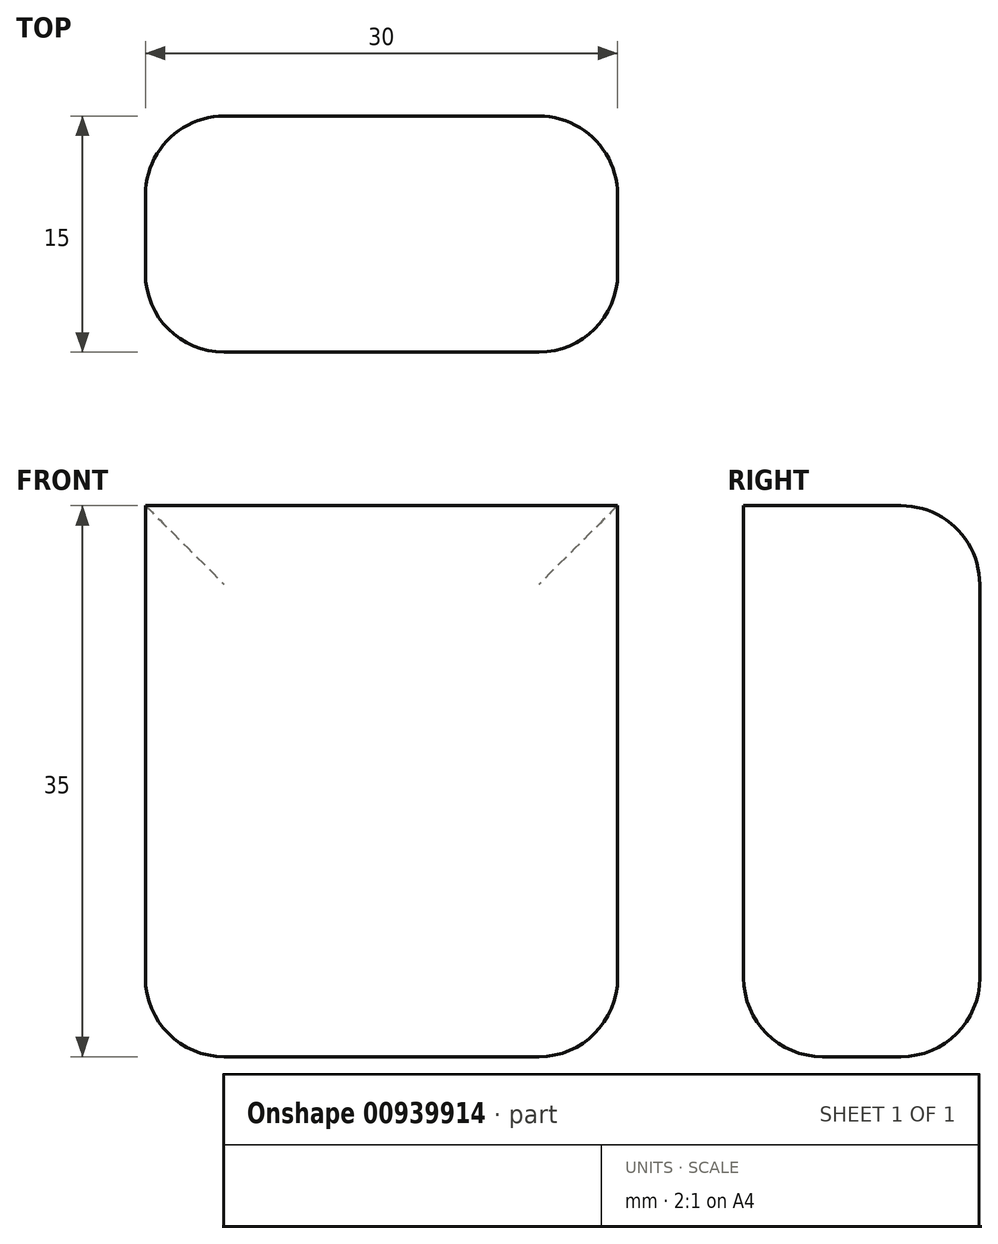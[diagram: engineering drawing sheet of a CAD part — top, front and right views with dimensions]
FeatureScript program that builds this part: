
annotation { "Feature Type Name" : "Feature", "Feature Type Description" : "" }
export const myFeature = defineFeature(function(context is Context, id is Id, definition is map)
    precondition{}
    {
        {
            var Q0;
            Q0=qCreatedBy(makeId("Front.planeOp"),FACE);
            var sketch = newSketch(context, id + "F0", { "sketchPlane" : qUnion([Q0])});
            skLineSegment(sketch, "E0.bottom", {"start": v(-15, 17.5) * mm, "end": v(15, 17.5) * mm});
            skLineSegment(sketch, "E0.top", {"start": v(-15, -17.5) * mm, "end": v(15, -17.5) * mm});
            skLineSegment(sketch, "E0.left", {"start": v(-15, 17.5) * mm, "end": v(-15, -17.5) * mm});
            skLineSegment(sketch, "E0.right", {"start": v(15, 17.5) * mm, "end": v(15, -17.5) * mm});
            skPoint(sketch, "E0.middle", {"position": v(0, 0) * mm});
            skSolve(sketch);
        }
        {
            var Q0;
            Q0 = qSketchRegion(id + "F0", true);
            extrude(context, id + "F1", {"entities" : qUnion([Q0]), "depth" : 15 * mm, "offsetDistance" : 25 * mm});
        }
        {
            var Q0;
            Q0=makeQuery(id+"F1.opExtrude","CAP_EDGE",EDGE,{"disambiguationData":[OSD([sQuery(id+"F0.wireOp",EDGE,"E0.top")])],"isStart":false});
            var Q1;
            Q1=makeQuery(id+"F1.opExtrude","CAP_EDGE",EDGE,{"disambiguationData":[OSD([sQuery(id+"F0.wireOp",EDGE,"E0.top")])],"isStart":true});
            var Q2;
            Q2=makeQuery(id+"F1.opExtrude","SWEPT_EDGE",EDGE,{"disambiguationData":[OSD([sQuery(id+"F0.wireOp",EDGE,"E0.top"),sQuery(id+"F0.wireOp",EDGE,"E0.left")])]});
            var Q3;
            Q3=makeQuery(id+"F1.opExtrude","SWEPT_EDGE",EDGE,{"disambiguationData":[OSD([sQuery(id+"F0.wireOp",EDGE,"E0.top"),sQuery(id+"F0.wireOp",EDGE,"E0.right")])]});
            var Q4;
            Q4=makeQuery(id+"F1.opExtrude","CAP_EDGE",EDGE,{"disambiguationData":[OSD([sQuery(id+"F0.wireOp",EDGE,"E0.right")])],"isStart":false});
            var Q5;
            Q5=makeQuery(id+"F1.opExtrude","CAP_EDGE",EDGE,{"disambiguationData":[OSD([sQuery(id+"F0.wireOp",EDGE,"E0.left")])],"isStart":false});
            var Q6;
            Q6=makeQuery(id+"F1.opExtrude","CAP_EDGE",EDGE,{"disambiguationData":[OSD([sQuery(id+"F0.wireOp",EDGE,"E0.right")])],"isStart":true});
            var Q7;
            Q7=makeQuery(id+"F1.opExtrude","CAP_FACE",FACE,{"disambiguationData":[OSD([sQuery(id+"F0.wireOp",EDGE,"E0.bottom"),sQuery(id+"F0.wireOp",EDGE,"E0.top"),sQuery(id+"F0.wireOp",EDGE,"E0.left"),sQuery(id+"F0.wireOp",EDGE,"E0.right")])],"isStart":true});
            fillet(context, id + "F2", {"entities" : qUnion([Q0, Q1, Q2, Q3, Q4, Q5, Q6, Q7]), "radius" : 5 * mm, "tangentPropagation" : true, "allowEdgeOverflow" : false});
        }
    });
